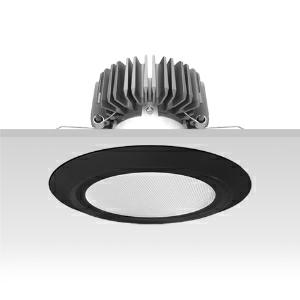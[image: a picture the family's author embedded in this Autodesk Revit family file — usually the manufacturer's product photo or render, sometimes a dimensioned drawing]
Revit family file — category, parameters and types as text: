
# Revit family: 3f_filippi_-_3f_reno_bianco_ampio_3f_filippi_-_30671_a01049_-_3f_reno_200_wh_2000-840_dali_wide___smp_bk_e788
name_source: partatom
category: Lighting Fixtures
units: mm (PartAtom-declared; Revit-internal decimal feet)

## family parameters
Cut with Voids When Loaded = No
Host = Face
Light Source = No
Part Type = Normal
Room Calculation Point = No
Round Connector Dimension = Use Diameter
Shared = No

## types (1)
- 3F Filippi - 3F Reno Bianco Ampio (1 x LED, 1723 lm, 20 W, 4000 K)
    Apparent Load = 20 VA
    Approval mark = CE
    CIE Flux Codes = 74 92 98 100 100
    Color Rendering = 80
    Color Temperature = 4000 K
    Control Gear = Electronic transformer
    Default Elevation = 1800 mm
    Description = ILLUMINOTECHNICAL
Luminous efficiency 100% (DLOR 100%, ULOR 0%).
Initial luminous flux of the luminaire 1723 lm.
Direct symmetric wide distribution.
Installation Interdistance Transv.D = 1.06 x hu - Long.D = 1.04 x hu.
Average luminance <3000 cd/m² for radial angles >65°.
Tabular UGR (CIE 117 - 4H-8H; S=0.25H; 70/50/20): RUG 21.4 - 21.3.
Beam angle: 70° - 69°.
Luminous efficacy 86 lm/W.
Lifetime (L90/B10): 30000 h. (tq+25°C)
Lifetime (L85/B10): 50000 h. (tq+25°C)
Lifetime (L70/B10): 80000 h. (tq+25°C)
Sudden decreased luminous flux after 50000 hours: 0% (C0).
Photobiological safety in compliance with IEC/TR 62778: RG0 risk exempt, (IEC 62471).
In compliance with IEC/EN 62722-2-1 - IEC/EN 62717 standards.

SOURCE
Compact LED module 2000/840.
Energy efficiency class (UE 2019/2020 - UE 2019/2015): D.
CIE 13.3 Colour rendering index: CRI >80 (R9 <50%).
IES TM-30 Fidelity Index: Rf = 84 Rg = 95.
CCT nominal colour temperature 4000 K.
Colour initial tolerance (MacAdam): SDCM 3.
Zhaga Book 3 compliant.

MECHANICAL
Passive heat dissipator in die-casting aluminium, oversized, for optimum thermal management of the LED module.
Parabolic element with graduated/concentric rings in white polycarbonate.
Transparent external lens with glossy and satin differentiated surfaces, with a cooling and anti-insect system in methacrylate (PMMA).
Fastening spring clips in stainless steel.
Dimensions: diameter 226 mm, height 146 mm. Weight 1.1 kg.
IP44 protection degree for exposed part, IP20 for recessed part.
Mechanical strength to impacts IK05 (0.7 joule).
Glow-wire test resistance 650°C.

ELECTRICAL
Wiring on a separate unit.
Halogen Free DALI-2 DATI (Parts 251, 252, 253), PUSH-DIM, electronic wiring 230V-50/60Hz, power factor 0.90 at full load, THD <25%, constant output current, SELV, class II, 1 driver, 1 DALI addresse.
Power of the luminaire 20 W.
ENEC - CE.
SAFE FLICKER: PstLM=<1 and SVM=<0.4 (IEC TR 61547-1 and IEC TR 63158), to ensure a more comfortable and safe light.
Luminaire compliant with EN 60598-2-22 for power supply from a centralised emergency system CPSS (Central Power Supply System), not incorporated in the luminaire - high risk areas excluded. The default power and flux are 100% in AC and 100% in DC.
Ambient temperature from 0°C to +25°C.
Temperature class T6 max 85°C.
Relative humidity UR: <85%.

INSTALLATION
Pull-up recessed fitting.
False ceiling carving: 200 mm.
All accessories dedicated to this product are available on the Catalog and on our website www.3F-Filippi.com.

ACCESSORIES
A01049 - Anti-glare microprismatic SMP diffuser in methacrylate (PMMA), locked and in line with the trim, in black polycarbonate.

APPLICATIONS
Suitable product for food production plants (HACCP), IFS (Food Version 6), BRC (GSFS Food Version 7).
Environments: architectural, commercial, exhibition areas, transit areas, corridors, shops, display windows, service areas.
In false ceilings with narrow voids.

LIGHT MANAGEMENT
Recommended minimum setting: 10%.
The luminaire, equipped with (DALI-2 DATI) driver, can be controlled manually with 3F Easy Dim technology or automatically/manually with wired or wireless DALI/D2D control systems.
The D2D driver guarantees interoperability with other devices with the same certification by making the following information available:
Device Data (Part 251), Energy Report (Part 252), Diagnosis & Maintenance (Part 253).
In electrical systems without a regulation system (manual or automatic) and DALI bus, a suitable jumper must be made on the DA-DA terminals of the appliance.

WARNING
Luminaire designed for disposal/recycling at end-of-life.
Replaceable (LED only) light source by a professional. Replaceable control gear by a professional.
    Height = 0 mm  [stored 0 ft]
    Lamp = 1 x LED
    Lamp Light Flux = 1723 lm
    Lamp Power = 20 W
    Lamp count = 1
    Length = 226 mm
    Lifetime = 50000 h
    Luminous efficacy = 86 lm/W
    Manufacturer = 3F Filippi
    ModVariant = No
    Model = 3F Filippi - 30671+A01049 - 3F Reno 200 WH 2000-840 DALI WIDE + SMP BK
    Mounting Place = Ceiling
    Mounting Type = Recessed
    Number of Poles = 1
    OnlyDefault = Yes
    Power Factor = 1
    Product Name = 3F Filippi - 3F Reno Bianco Ampio
    Product group = recessed luminaire
    ProductGroupID = 4
    Protection Class = Protection class II
    Protection Degree = IP 20
    RLX_Detail_Level = 1
    RLX_Emergency_Light_Flux = 0 lm
    RLX_Emergency_Type = 0
    RLX_Emergency_Type_DB = No
    RlxData = <blob elided: 99741 chars, md5=0d4fac9e>
    Socket = socket
    Standby Power = 0 W
    System Light Flux = 1723 lm
    System Power = 20 W
    Type Comments = Product without accessories
    Type Image = 3ffilippi_3f_reno_200_bk_vs_smp.jpg
    URL = http://relux.com
    VarID = ---
    Voltage = 0 V
    Weight = 0.00 kg
    Width = 0 mm  [stored 0 ft]

note: [stored X ft] marks values corroborated as IEEE doubles in the binary element streams (Revit-internal decimal feet)

## geometry (parser evidence)
native form markers: Blend x4, Sweep x11
no freeform markers — native parametric forms only
